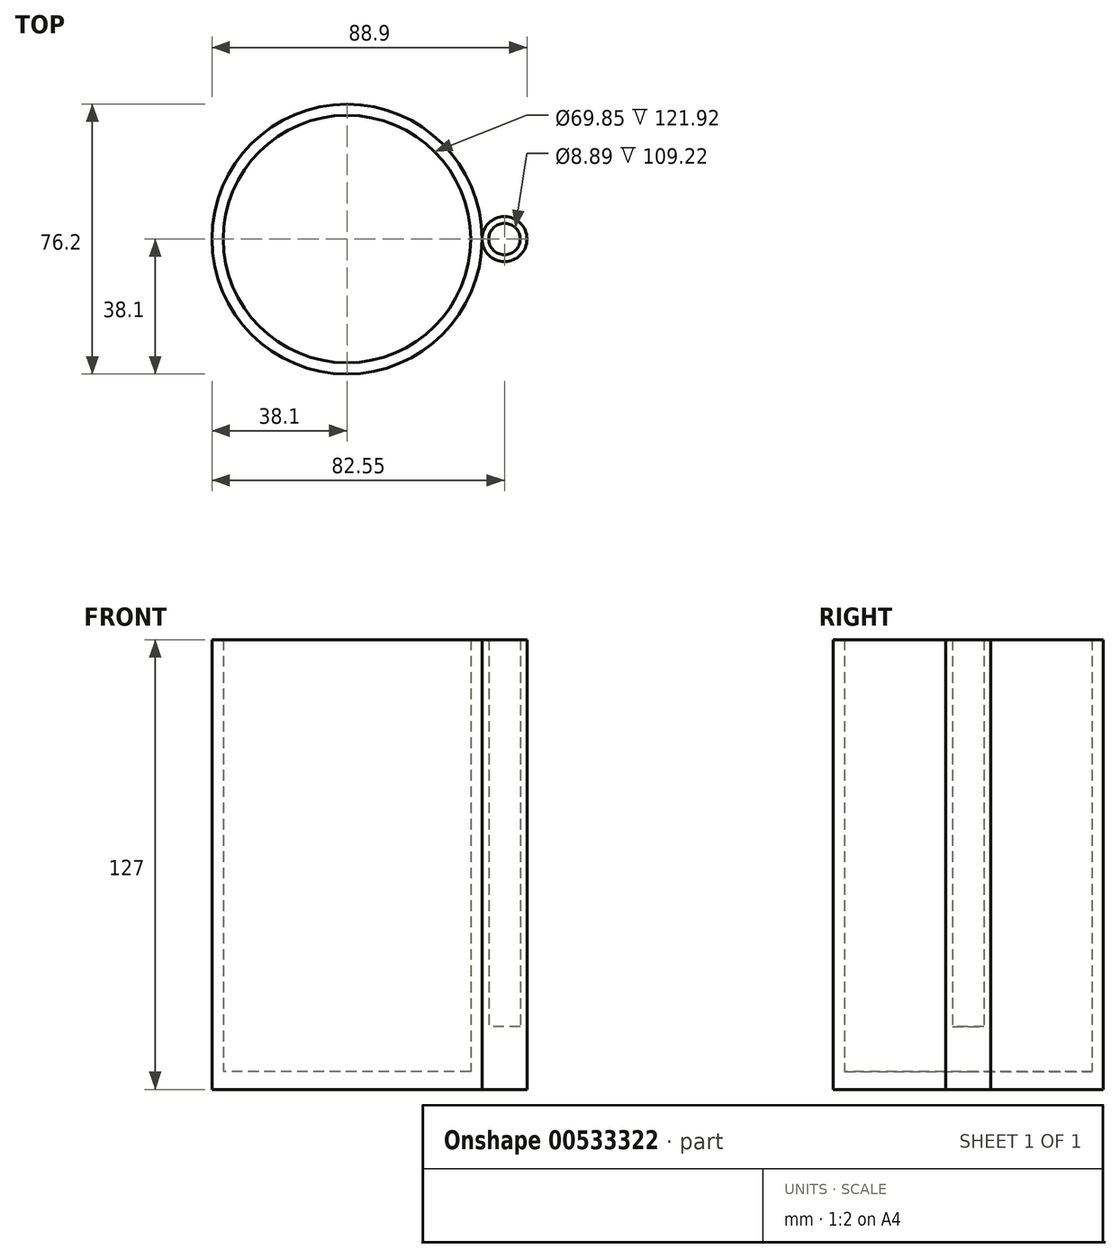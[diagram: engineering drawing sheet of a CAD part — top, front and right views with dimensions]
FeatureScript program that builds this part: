
annotation { "Feature Type Name" : "Feature", "Feature Type Description" : "" }
export const myFeature = defineFeature(function(context is Context, id is Id, definition is map)
    precondition{}
    {
        {
            var Q0;
            Q0=qCreatedBy(makeId("Top.planeOp"),FACE);
            var sketch = newSketch(context, id + "F0", { "sketchPlane" : qUnion([Q0])});
            skCircle(sketch, "E0", {"center": v(0, 0) * mm, "radius": 38.1 * mm});
            skPoint(sketch, "E1", {"position": v(38.1, 0) * mm});
            skCircle(sketch, "E2", {"center": v(44.45, 0) * mm, "radius": 6.35 * mm});
            skCircle(sketch, "E3", {"center": v(44.45, 0) * mm, "radius": 4.45 * mm});
            skCircle(sketch, "E4", {"center": v(0, 0) * mm, "radius": 34.93 * mm});
            skSolve(sketch);
        }
        {
            var Q0;
            Q0 = qSketchRegion(id + "F0", true);
            extrude(context, id + "F1", {"entities" : qUnion([Q0]), "depth" : 127 * mm, "offsetDistance" : 25.4 * mm});
        }
        {
            var Q0;
            Q0=makeQuery(id+"F0.imprint","IMPRINT",FACE,{"disambiguationData":[TD([[makeQuery(id+"F0.imprint","IMPRINT",EDGE,{"derivedFrom":sQuery(id+"F0.wireOp",EDGE,"E4")}),1.0]])]});
            extrude(context, id + "F2", {"entities" : qUnion([Q0]), "operationType" : NewBodyOperationType.ADD, "depth" : 5.08 * mm, "offsetDistance" : 25.4 * mm});
        }
        {
            var Q0;
            Q0=makeQuery(id+"F0.imprint","IMPRINT",FACE,{"disambiguationData":[TD([[makeQuery(id+"F0.imprint","IMPRINT",EDGE,{"derivedFrom":sQuery(id+"F0.wireOp",EDGE,"E3")}),1.0]])]});
            extrude(context, id + "F3", {"entities" : qUnion([Q0]), "operationType" : NewBodyOperationType.ADD, "depth" : 17.78 * mm, "offsetDistance" : 25.4 * mm});
        }
    });
